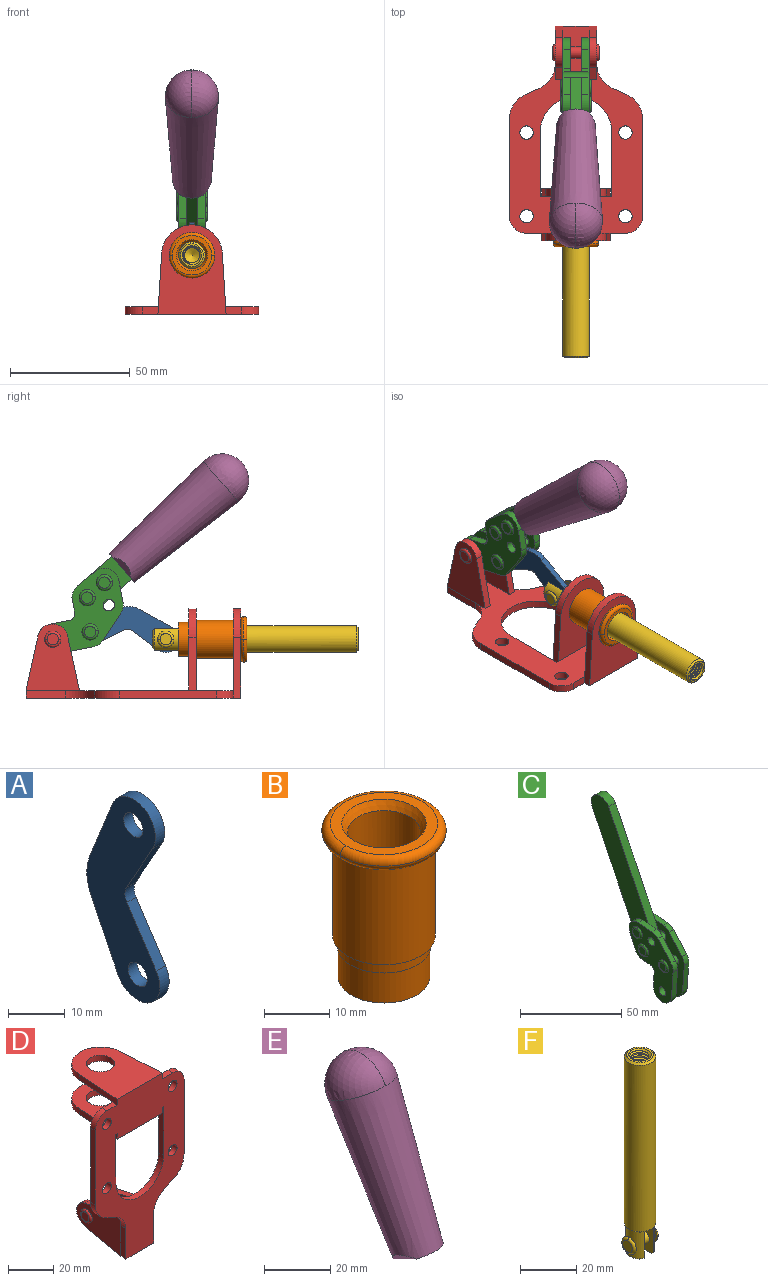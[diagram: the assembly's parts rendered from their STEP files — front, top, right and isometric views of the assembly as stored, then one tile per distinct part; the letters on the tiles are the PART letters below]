
ASSEMBLY  parts=6 mates=6
PART A: 12 faces, bbox 2.3x18.2x42.8 mm
  f0: cylinder r=2.4mm len=4.8mm, axis (1,0,0), area 34.9mm2, adj f4,f11
  f1: cylinder r=10.41mm len=8.47mm, axis (1,0,0), area 20.2mm2, adj f4,f9,f10,f11
  f2: cylinder r=3.05mm len=3.16mm, axis (1,0,0), area 7.7mm2, adj f4,f6,f7,f11
  f3: cylinder r=2.4mm len=4.8mm, axis (1,0,0), area 34.9mm2, adj f4,f11
  f4: plane 42.81x18.23mm, normal (-1,0,0), area 414.1mm2, adj f0,f1,f2,f3,f5,f6,f7,f8
  f5: cylinder r=5.54mm len=10.67mm, axis (1,0,0), area 41.8mm2, adj f4,f6,f10,f11
  f6: plane 11.66x6.53mm, normal (0,-0.87,-0.49), area 30.9mm2, adj f2,f4,f5,f11
  f7: plane 11.17x7.33mm, normal (0,-0.84,0.55), area 30.9mm2, adj f2,f4,f8,f11
  f8: cylinder r=5.54mm len=10.51mm, axis (1,0,0), area 41.8mm2, adj f4,f7,f9,f11
  f9: plane 13.67x6.67mm, normal (0,0.9,-0.44), area 35.1mm2, adj f1,f4,f8,f11
  f10: plane 14.1x5.7mm, normal (0,0.93,0.37), area 35.1mm2, adj f1,f4,f5,f11
  f11: plane 42.81x18.23mm, normal (1,0,0), area 414.1mm2, adj f0,f1,f2,f3,f5,f6,f7,f8
PART B: 15 faces, bbox 20.6x20.6x28.7 mm
  f0: torus R=8.26mm, axis (0,0,1), area 56.8mm2, adj f1,f10,f12
  f1: torus R=8.26mm, axis (0,0,1), area 56.8mm2, adj f0,f6,f13
  f2: cylinder r=5.59mm len=25.91mm, axis (0,0,1), area 909.6mm2, adj f3,f4
  f3: cone r=6.86mm half-angle=45deg, axis (0,0,-1), area 70.2mm2, adj f2,f14
  f4: cone r=6.47mm half-angle=30deg, axis (0,0,1), area 66.7mm2, adj f2,f13
  f5: cylinder r=7.04mm len=14.07mm, axis (0,0,1), area 252.6mm2, adj f11,f14
  f6: torus R=8.26mm, axis (0,0,1), area 56.8mm2, adj f1,f12,f13
  f7: cylinder r=7.16mm len=14.33mm, axis (0,0,1), area 91.5mm2, adj f9,f11
  f8: cylinder r=7.86mm len=18.42mm, axis (0,0,1), area 909.6mm2, adj f9,f10
  f9: plane 15.72x15.72mm, normal (0,0,-1), area 33mm2, adj f7,f8
  f10: plane 16.51x16.51mm, normal (0,0,-1), area 19.9mm2, adj f0,f8,f12
  f11: plane 14.33x14.33mm, normal (0,0,-1), area 5.7mm2, adj f5,f7
  f12: torus R=8.26mm, axis (0,0,1), area 56.8mm2, adj f0,f6,f10
  f13: plane 16.51x16.51mm, normal (0,0,1), area 82.7mm2, adj f1,f4,f6
  f14: plane 14.07x14.07mm, normal (0,0,-1), area 7.8mm2, adj f3,f5
PART C: 59 faces, bbox 12.9x60.2x99.6 mm
  f0: torus R=2.39mm, axis (-1,0,0), area 14.9mm2, adj f20,f43,f51
  f1: torus R=2.39mm, axis (-1,0,0), area 14.9mm2, adj f19,f42,f51
  f2: torus R=2.39mm, axis (-1,0,0), area 14.9mm2, adj f18,f35,f51
  f3: torus R=2.39mm, axis (-1,0,0), area 14.9mm2, adj f14,f17,f23
  f4: torus R=2.39mm, axis (-1,0,0), area 14.9mm2, adj f13,f16,f23
  f5: torus R=2.39mm, axis (-1,0,0), area 14.9mm2, adj f12,f15,f23
  f6: cylinder r=2.39mm len=4.78mm, axis (1,0,0), area 46.5mm2, adj f48,f50,f51
  f7: cylinder r=2.39mm len=4.78mm, axis (1,0,0), area 46.5mm2, adj f50,f51
  f8: cylinder r=6.35mm len=12.68mm, axis (1,0,0), area 61.8mm2, adj f38,f39,f50,f51
  f9: cylinder r=2.39mm len=4.78mm, axis (-1,0,0), area 70.5mm2, adj f46,f50
  f10: cylinder r=2.39mm len=4.78mm, axis (-1,0,0), area 46.5mm2, adj f23,f45,f46
  f11: cylinder r=2.39mm len=4.78mm, axis (-1,0,0), area 46.5mm2, adj f23,f46
  f12: plane 4.78x4.78mm, normal (1,0,0), area 17.9mm2, adj f5,f15
  f13: plane 4.78x4.78mm, normal (1,0,0), area 17.9mm2, adj f4,f16
  f14: plane 4.78x4.78mm, normal (1,0,0), area 17.9mm2, adj f3,f17
  f15: torus R=2.39mm, axis (-1,0,0), area 14.9mm2, adj f5,f12,f23
  f16: torus R=2.39mm, axis (-1,0,0), area 14.9mm2, adj f4,f13,f23
  f17: torus R=2.39mm, axis (-1,0,0), area 14.9mm2, adj f3,f14,f23
  f18: plane 4.78x4.78mm, normal (-1,0,0), area 17.9mm2, adj f2,f35
  f19: plane 4.78x4.78mm, normal (-1,0,0), area 17.9mm2, adj f1,f42
  f20: plane 4.78x4.78mm, normal (-1,0,0), area 17.9mm2, adj f0,f43
  f21: plane 2.26x0.2mm, normal (1,0,0), area 0.2mm2, adj f31,f44
  f22: plane 2.26x0.2mm, normal (-1,0,0), area 0.2mm2, adj f41,f44
  f23: plane 39.37x30.77mm, normal (1,0,0), area 565.5mm2, adj f3,f4,f5,f10,f11,f15,f16,f17
  f24: cylinder r=6.1mm len=4.15mm, axis (-1,0,0), area 14.7mm2, adj f23,f25,f32,f46
  f25: plane 10.25x9.01mm, normal (0,-0.75,0.66), area 42.3mm2, adj f23,f24,f26,f46
  f26: cylinder r=6.35mm len=4.64mm, axis (-1,0,0), area 15.6mm2, adj f23,f25,f27,f46
  f27: plane 15.84x3.1mm, normal (0,-1,-0.07), area 49.2mm2, adj f23,f26,f28,f46
  f28: cylinder r=6.35mm len=12.68mm, axis (-1,0,0), area 61.8mm2, adj f23,f27,f29,f46
  f29: plane 8.11x3.1mm, normal (0,1,0.07), area 25.2mm2, adj f23,f28,f30,f46
  f30: cylinder r=3.05mm len=3.25mm, axis (-1,0,0), area 14.8mm2, adj f23,f29,f31,f46
  f31: plane 5.99x3.1mm, normal (0,0.07,-1), area 18.6mm2, adj f21,f23,f30,f44,f46
  f32: plane 9.5x3.1mm, normal (0,-0.07,1), area 29.5mm2, adj f23,f24,f33,f46,f47
  f33: cylinder r=6.1mm len=8.63mm, axis (-1,0,0), area 39.1mm2, adj f23,f32,f34,f47
  f34: plane 8.65x3.96mm, normal (0,0.91,-0.42), area 29.5mm2, adj f23,f33,f44,f47
  f35: torus R=2.39mm, axis (-1,0,0), area 14.9mm2, adj f2,f18,f51
  f36: plane 10.25x9.01mm, normal (0,-0.75,0.66), area 42.3mm2, adj f37,f49,f50,f51
  f37: cylinder r=6.35mm len=4.64mm, axis (1,0,0), area 15.6mm2, adj f36,f38,f50,f51
  f38: plane 15.84x3.1mm, normal (0,-1,-0.07), area 49.2mm2, adj f8,f37,f50,f51
  f39: plane 8.11x3.1mm, normal (0,1,0.07), area 25.2mm2, adj f8,f40,f50,f51
  f40: cylinder r=3.05mm len=3.25mm, axis (1,0,0), area 14.8mm2, adj f39,f41,f50,f51
  f41: plane 5.99x3.1mm, normal (0,0.07,-1), area 18.6mm2, adj f22,f40,f44,f50,f51
  f42: torus R=2.39mm, axis (-1,0,0), area 14.9mm2, adj f1,f19,f51
  f43: torus R=2.39mm, axis (-1,0,0), area 14.9mm2, adj f0,f20,f51
  f44: cylinder r=6.35mm len=12.12mm, axis (-1,0,0), area 128.9mm2, adj f21,f22,f23,f31,f34,f41,f46,f47
  f45: plane 2.65x1.35mm, normal (1,0,0), area 1mm2, adj f10,f55
  f46: plane 39.08x20.42mm, normal (-1,0,0), area 412.5mm2, adj f9,f10,f11,f24,f25,f26,f27,f28
  f47: plane 77.62x39.82mm, normal (1,0,0), area 850mm2, adj f32,f33,f34,f44,f53,f54,f55
  f48: plane 2.65x1.35mm, normal (-1,0,0), area 1mm2, adj f6,f55
  f49: cylinder r=6.1mm len=4.15mm, axis (1,0,0), area 14.7mm2, adj f36,f50,f51,f56
  f50: plane 39.08x20.42mm, normal (1,0,0), area 412.5mm2, adj f6,f7,f8,f9,f36,f37,f38,f39
  f51: plane 39.37x30.77mm, normal (-1,0,0), area 565.5mm2, adj f0,f1,f2,f6,f7,f8,f35,f36
  f52: plane 8.65x3.96mm, normal (0,0.91,-0.42), area 29.5mm2, adj f44,f51,f57,f58
  f53: plane 68.49x33.4mm, normal (0,0.9,-0.44), area 358.1mm2, adj f44,f47,f54,f58
  f54: cylinder r=6.35mm len=12.06mm, axis (1,0,0), area 93.7mm2, adj f47,f53,f55,f58
  f55: plane 68.49x33.4mm, normal (0,-0.9,0.44), area 358.1mm2, adj f44,f45,f46,f47,f48,f50,f54,f58
  f56: plane 9.5x3.1mm, normal (0,-0.07,1), area 29.5mm2, adj f49,f50,f51,f57,f58
  f57: cylinder r=6.1mm len=8.63mm, axis (1,0,0), area 39.1mm2, adj f51,f52,f56,f58
  f58: plane 77.62x39.82mm, normal (-1,0,0), area 850mm2, adj f44,f52,f53,f54,f55,f56,f57
PART D: 55 faces, bbox 55.7x37.4x89.8 mm
  f0: torus R=2.41mm, axis (-1,0,0), area 15mm2, adj f11,f15,f25
  f1: torus R=2.41mm, axis (-1,0,0), area 15mm2, adj f10,f12,f22
  f2: cylinder r=2.78mm len=5.56mm, axis (0,-1,0), area 54.2mm2, adj f30,f54
  f3: cylinder r=14.99mm len=29.97mm, axis (0,-1,0), area 145.9mm2, adj f30,f49,f53,f54
  f4: cylinder r=2.78mm len=5.56mm, axis (0,-1,0), area 54.2mm2, adj f30,f54
  f5: cylinder r=2.78mm len=5.56mm, axis (0,-1,0), area 54.2mm2, adj f30,f54
  f6: cylinder r=2.78mm len=5.56mm, axis (0,-1,0), area 54.2mm2, adj f30,f54
  f7: cylinder r=6.35mm len=12.7mm, axis (0,0,1), area 123.6mm2, adj f27,f51
  f8: cylinder r=6.35mm len=12.7mm, axis (0,0,-1), area 124.7mm2, adj f21,f35
  f9: cylinder r=2.41mm len=11.18mm, axis (-1,0,0), area 169.4mm2, adj f16,f19
  f10: plane 4.83x4.83mm, normal (1,0,0), area 18.3mm2, adj f1,f12
  f11: plane 4.83x4.83mm, normal (-1,0,0), area 18.3mm2, adj f0,f15
  f12: torus R=2.41mm, axis (-1,0,0), area 15mm2, adj f1,f10,f22
  f13: cylinder r=6.35mm len=12.41mm, axis (1,0,0), area 53.4mm2, adj f18,f19,f22,f23
  f14: cylinder r=6.35mm len=12.41mm, axis (-1,0,0), area 53.4mm2, adj f16,f17,f24,f25
  f15: torus R=2.41mm, axis (-1,0,0), area 15mm2, adj f0,f11,f25
  f16: plane 27.86x22.35mm, normal (1,0,0), area 425.4mm2, adj f9,f14,f17,f24,f30
  f17: plane 22.86x4.97mm, normal (0,0.21,0.98), area 72.5mm2, adj f14,f16,f25,f30
  f18: plane 22.86x4.97mm, normal (0,0.21,0.98), area 72.5mm2, adj f13,f19,f22,f30
  f19: plane 27.86x22.35mm, normal (-1,0,0), area 425.4mm2, adj f9,f13,f18,f23,f30
  f20: cylinder r=12.7mm len=25.35mm, axis (0,0,-1), area 119.8mm2, adj f21,f34,f35,f36
  f21: plane 34.21x28.07mm, normal (0,0,-1), area 702.4mm2, adj f8,f20,f30,f34,f36
  f22: plane 27.96x22.45mm, normal (1,0,0), area 407.2mm2, adj f1,f12,f13,f18,f23,f30,f42,f43
  f23: plane 22.86x4.97mm, normal (0,0.21,-0.98), area 72.5mm2, adj f13,f19,f22,f44
  f24: plane 22.86x4.97mm, normal (0,0.21,-0.98), area 72.5mm2, adj f14,f16,f25,f44
  f25: plane 27.86x22.35mm, normal (-1,0,0), area 407.1mm2, adj f0,f14,f15,f17,f24,f30,f45,f46
  f26: plane 3.1x0.95mm, normal (0,0,-1), area 2.7mm2, adj f30,f49,f50,f54
  f27: plane 34.21x28.07mm, normal (0,0,1), area 702.4mm2, adj f7,f28,f30,f50,f52
  f28: cylinder r=12.7mm len=25.35mm, axis (0,0,1), area 118.8mm2, adj f27,f50,f51,f52
  f29: plane 3.1x0.95mm, normal (0,0,-1), area 2.7mm2, adj f30,f52,f53,f54
  f30: plane 86.54x55.63mm, normal (0,1,0), area 2362.9mm2, adj f2,f3,f4,f5,f6,f16,f17,f18
  f31: plane 40.56x3.1mm, normal (-1,0,0), area 125.7mm2, adj f30,f32,f48,f54
  f32: cylinder r=7.11mm len=7.11mm, axis (0,-1,0), area 34.6mm2, adj f30,f31,f33,f54
  f33: plane 6.67x3.1mm, normal (0,0,1), area 20.4mm2, adj f30,f32,f34,f54
  f34: plane 25.39x3.13mm, normal (-1,0.06,0), area 79.5mm2, adj f20,f21,f33,f35,f54
  f35: plane 37.31x28.45mm, normal (0,0,1), area 789.9mm2, adj f8,f20,f34,f36,f54
  f36: plane 25.39x3.13mm, normal (1,0.06,0), area 79.5mm2, adj f20,f21,f35,f37,f54
  f37: plane 6.67x3.1mm, normal (0,0,1), area 20.4mm2, adj f30,f36,f38,f54
  f38: cylinder r=7.11mm len=7.11mm, axis (0,-1,0), area 34.6mm2, adj f30,f37,f39,f54
  f39: plane 40.56x3.1mm, normal (1,0,0), area 125.7mm2, adj f30,f38,f40,f54
  f40: cylinder r=11.18mm len=10.16mm, axis (0,-1,0), area 39.5mm2, adj f30,f39,f41,f54
  f41: plane 6.09x3.1mm, normal (0.42,0,-0.91), area 20.8mm2, adj f30,f40,f42,f54
  f42: cylinder r=11.18mm len=9.41mm, axis (0,-1,0), area 37.2mm2, adj f22,f30,f41,f43,f54
  f43: plane 16.5x3.1mm, normal (1,0,0), area 51.1mm2, adj f22,f42,f44,f54
  f44: plane 17.37x3.1mm, normal (0,0,-1), area 53.8mm2, adj f23,f24,f30,f43,f45,f54
  f45: plane 16.5x3.1mm, normal (-1,0,0), area 51.1mm2, adj f25,f44,f46,f54
  f46: cylinder r=11.18mm len=9.41mm, axis (0,-1,0), area 37.2mm2, adj f25,f30,f45,f47,f54
  f47: plane 6.09x3.1mm, normal (-0.42,0,-0.91), area 20.8mm2, adj f30,f46,f48,f54
  f48: cylinder r=11.18mm len=10.16mm, axis (0,-1,0), area 39.5mm2, adj f30,f31,f47,f54
  f49: plane 26.54x3.1mm, normal (-1,0,0), area 82.3mm2, adj f3,f26,f30,f54
  f50: plane 25.39x3.1mm, normal (1,0.06,0), area 78.8mm2, adj f26,f27,f28,f51,f54
  f51: plane 37.31x28.45mm, normal (0,0,-1), area 789.9mm2, adj f7,f28,f50,f52,f54
  f52: plane 25.39x3.1mm, normal (-1,0.06,0), area 78.8mm2, adj f27,f28,f29,f51,f54
  f53: plane 26.54x3.1mm, normal (1,0,0), area 82.3mm2, adj f3,f29,f30,f54
  f54: plane 89.66x55.63mm, normal (0,-1,0), area 2678.5mm2, adj f2,f3,f4,f5,f6,f26,f29,f31
PART E: 11 faces, bbox 22.3x42.6x64.5 mm
  f0: sphere r=11.13mm, area 411.4mm2, adj f1,f8
  f1: cone r=11.11mm half-angle=3.3deg, axis (0,0.44,0.9), area 3251.8mm2, adj f0,f7,f8,f9,f10
  f2: cylinder r=6.16mm len=11.7mm, axis (1,0,0), area 89.5mm2, adj f3,f4,f5,f6
  f3: plane 60.23x36.75mm, normal (-1,0,0), area 763.6mm2, adj f2,f4,f6,f10
  f4: plane 51.37x25.05mm, normal (0,0.9,-0.44), area 264.2mm2, adj f2,f3,f5,f10
  f5: plane 60.23x36.75mm, normal (1,0,0), area 763.6mm2, adj f2,f4,f6,f10
  f6: plane 51.37x25.05mm, normal (0,-0.9,0.44), area 264.2mm2, adj f2,f3,f5,f10
  f7: plane 9.95x5.95mm, normal (0.71,-0.31,-0.64), area 25.8mm2, adj f1,f10
  f8: sphere r=11.13mm, area 411.4mm2, adj f0,f1
  f9: plane 9.95x5.95mm, normal (-0.71,-0.31,-0.64), area 25.8mm2, adj f1,f10
  f10: plane 14.27x11.38mm, normal (0,-0.44,-0.9), area 106.7mm2, adj f1,f3,f4,f5,f6,f7,f9
PART F: 48 faces, bbox 12.6x11.1x86.1 mm
  f0: torus R=2.41mm, axis (-1,0,0), area 15mm2, adj f30,f32,f34
  f1: torus R=2.41mm, axis (-1,0,0), area 15mm2, adj f29,f31,f33
  f2: cylinder r=5.54mm len=72.39mm, axis (0,0,1), area 2518.5mm2, adj f3,f4,f42,f43
  f3: cone r=5.54mm half-angle=45deg, axis (0,0,1), area 7.6mm2, adj f2,f5,f41
  f4: cone r=5.54mm half-angle=45deg, axis (0,0,-1), area 34.9mm2, adj f2,f39
  f5: cylinder r=5.08mm len=11.48mm, axis (0,0,1), area 108.3mm2, adj f3,f7,f8,f41
  f6: cylinder r=2.41mm len=4.83mm, axis (-1,0,0), area 71.2mm2, adj f40,f41
  f7: cylinder r=2.41mm len=4.83mm, axis (-1,0,0), area 7.6mm2, adj f5,f34
  f8: cone r=5.08mm half-angle=45deg, axis (0,0,1), area 10.6mm2, adj f5,f37,f41
  f9: cone r=3.98mm half-angle=45deg, axis (0,0,1), area 17.6mm2, adj f27,f39,f45,f46,f47
  f10: cylinder r=2.41mm len=4.83mm, axis (-1,0,0), area 7.6mm2, adj f33,f38
  f11: cylinder r=3.2mm len=6.4mm, axis (0,0,1), area 78.4mm2, adj f12,f28,f44,f45,f47
  f12: cylinder r=3.2mm len=6.4mm, axis (0,0,1), area 10.5mm2, adj f11,f13,f45,f47
  f13: cylinder r=3.2mm len=6.4mm, axis (0,0,1), area 10.5mm2, adj f12,f14,f45,f47
  f14: cylinder r=3.2mm len=6.4mm, axis (0,0,1), area 10.5mm2, adj f13,f15,f45,f47
  f15: cylinder r=3.2mm len=6.4mm, axis (0,0,1), area 10.5mm2, adj f14,f16,f45,f47
  f16: cylinder r=3.2mm len=6.4mm, axis (0,0,1), area 10.5mm2, adj f15,f17,f45,f47
  f17: cylinder r=3.2mm len=6.4mm, axis (0,0,1), area 10.5mm2, adj f16,f18,f45,f47
  f18: cylinder r=3.2mm len=6.4mm, axis (0,0,1), area 10.5mm2, adj f17,f19,f45,f47
  f19: cylinder r=3.2mm len=6.4mm, axis (0,0,1), area 10.5mm2, adj f18,f20,f45,f47
  f20: cylinder r=3.2mm len=6.4mm, axis (0,0,1), area 10.5mm2, adj f19,f21,f45,f47
  f21: cylinder r=3.2mm len=6.4mm, axis (0,0,1), area 10.5mm2, adj f20,f22,f45,f47
  f22: cylinder r=3.2mm len=6.4mm, axis (0,0,1), area 10.5mm2, adj f21,f23,f45,f47
  f23: cylinder r=3.2mm len=6.4mm, axis (0,0,1), area 10.5mm2, adj f22,f24,f45,f47
  f24: cylinder r=3.2mm len=6.4mm, axis (0,0,1), area 10.5mm2, adj f23,f25,f45,f47
  f25: cylinder r=3.2mm len=6.4mm, axis (0,0,1), area 10.5mm2, adj f24,f26,f45,f47
  f26: cylinder r=3.2mm len=6.4mm, axis (0,0,1), area 10.5mm2, adj f25,f27,f45,f47
  f27: cylinder r=3.2mm len=6.4mm, axis (0,0,1), area 7.4mm2, adj f9,f26,f45,f47
  f28: cone r=3.2mm half-angle=60deg, axis (0,0,1), area 37.2mm2, adj f11
  f29: plane 4.83x4.83mm, normal (-1,0,0), area 18.3mm2, adj f1,f31
  f30: plane 4.83x4.83mm, normal (1,0,0), area 18.3mm2, adj f0,f32
  f31: torus R=2.41mm, axis (-1,0,0), area 15mm2, adj f1,f29,f33
  f32: torus R=2.41mm, axis (-1,0,0), area 15mm2, adj f0,f30,f34
  f33: plane 6.83x6.83mm, normal (1,0,0), area 18.3mm2, adj f1,f10,f31
  f34: plane 6.83x6.83mm, normal (-1,0,0), area 18.3mm2, adj f0,f7,f32
  f35: cone r=5.08mm half-angle=45deg, axis (0,0,1), area 10.6mm2, adj f36,f38,f40
  f36: plane 7.25x1.97mm, normal (0,0,-1), area 10mm2, adj f35,f40
  f37: plane 7.25x1.97mm, normal (0,0,-1), area 10mm2, adj f8,f41
  f38: cylinder r=5.08mm len=11.48mm, axis (0,0,1), area 108.3mm2, adj f10,f35,f40,f42
  f39: plane 9.55x9.55mm, normal (0,0,1), area 22mm2, adj f4,f9
  f40: plane 12.76x10.09mm, normal (1,0,0), area 95.7mm2, adj f6,f35,f36,f38,f42,f43
  f41: plane 12.76x10.09mm, normal (-1,0,0), area 95.7mm2, adj f3,f5,f6,f8,f37,f43
  f42: cone r=5.54mm half-angle=45deg, axis (0,0,1), area 7.6mm2, adj f2,f38,f40
  f43: plane 11.07x4.7mm, normal (0,0,-1), area 50.4mm2, adj f2,f40,f41
  f44: plane 0.89x0.62mm, normal (-1,0,0), area 0.3mm2, adj f11,f45,f46,f47
  f45: bspline ~24.8x7.63mm, area 266.6mm2, adj f9,f11,f12,f13,f14,f15,f16,f17
  f46: bspline ~24.87x7.63mm, area 73.6mm2, adj f9,f44,f45,f47
  f47: bspline ~24.98x7.63mm, area 272.5mm2, adj f9,f11,f12,f13,f14,f15,f16,f17
PLACE A rot(axis=(1,0,0),97.5deg) t=(0,12.88,2.22)mm
PLACE B rot(axis=(1,0,0),90deg) t=(0,9.43,0)mm
PLACE C rot(axis=(1,0,0),75deg) t=(0,4.15,9.14)mm
PLACE D rot(axis=(1,0,0),90deg) t=(0,9.43,0)mm fixed
PLACE E rot(axis=(1,0,0),75deg) t=(-0.04,4.15,9.14)mm
PLACE F rot(axis=(1,0,0),90deg) t=(0,9.81,0)mm
MATE revolute A.f5 <-> F.f6  axis (1,0,0) through (0,-5.67,24.61)mm
MATE revolute D.f0 <-> C.f7  axis (-1,0,0) through (0,41.52,24.61)mm
MATE revolute C.f4 <-> A.f3  axis (-1,0,0) through (0,25.94,27.64)mm
MATE fastened B.f2 <-> D.f7  axis (0,-1,0) through (0,-36.96,24.61)mm
MATE slider F.f2 <-> B.f2  axis (0,-1,0) through (0,-48.97,24.61)mm
MATE fastened C.f54 <-> E.f2  axis (-1,0,0) through (-2.35,-30.37,91.94)mm
